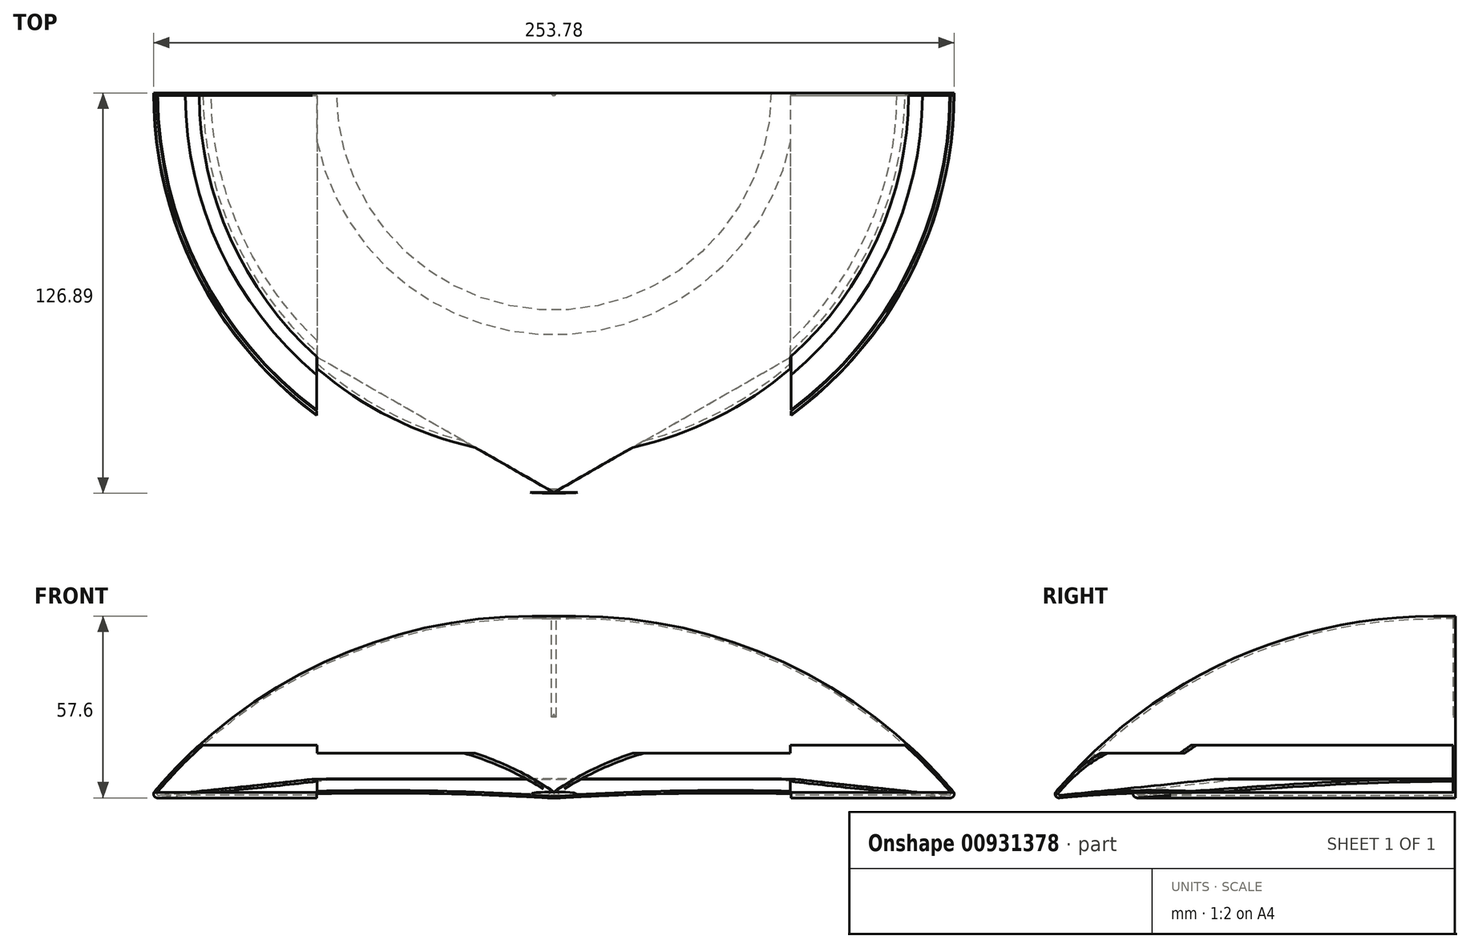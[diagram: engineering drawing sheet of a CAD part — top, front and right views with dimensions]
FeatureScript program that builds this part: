
annotation { "Feature Type Name" : "Feature", "Feature Type Description" : "" }
export const myFeature = defineFeature(function(context is Context, id is Id, definition is map)
    precondition{}
    {
        {
            var Q0;
            Q0=qCreatedBy(makeId("Right.planeOp"),FACE);
            var sketch = newSketch(context, id + "F0", { "sketchPlane" : qUnion([Q0])});
            skLineSegment(sketch, "E0", {"start": v(0, 0) * mm, "end": v(0, 55) * mm});
            skLineSegment(sketch, "E1", {"start": v(0, 0) * mm, "end": v(-107.97, 0) * mm});
            skArc(sketch, "E2", {"start": v(0, 55) * mm, "mid": v(-68.84, 41.9) * mm, "end": v(-125, 0) * mm});
            skLineSegment(sketch, "E3", {"start": v(0, 15) * mm, "end": v(0, 25) * mm});
            skLineSegment(sketch, "E4", {"start": v(-125, 0) * mm, "end": v(-75.8, 15) * mm});
            skLineSegment(sketch, "E5", {"start": v(-65.8, 25) * mm, "end": v(-75.8, 38.63) * mm});
            skLineSegment(sketch, "E6", {"start": v(0, 55) * mm, "end": v(-15, 40.73) * mm});
            skFitSpline(sketch, "E7", {"points": [v(-15, 40.73) * mm, v(-65.8, 25) * mm, v(-75.8, 15) * mm], "startDerivative": vector(-92.7, -22.01) * mm, "endDerivative": vector(-21.33, -30.33) * mm});
            skPoint(sketch, "E8.start.orphan", {"position": v(-125, 25) * mm});
            skPoint(sketch, "E9.end.orphan", {"position": v(-125, 15) * mm});
            skPoint(sketch, "E10.end.orphan", {"position": v(-15, 25) * mm});
            skArc(sketch, "E11.0", {"start": v(0.8, 55.77) * mm, "mid": v(-69, 42.71) * mm, "end": v(-125.87, 0.21) * mm});
            skLineSegment(sketch, "E11.1", {"start": v(0.8, -0.8) * mm, "end": v(0.8, 55.77) * mm});
            skLineSegment(sketch, "E11.2", {"start": v(0.8, -0.8) * mm, "end": v(-115.99, -0.8) * mm});
            skFitSpline(sketch, "E12", {"points": [v(-124.74, -0.86) * mm, v(-16.54, 15) * mm, v(0, 25) * mm], "startDerivative": vector(188.12, 18.56) * mm, "endDerivative": vector(41.4, 35.45) * mm});
            skFitSpline(sketch, "E13.0", {"points": [v(-124.66, -1.66) * mm, v(-116.82, -0.88) * mm, v(-101.14, 0.66) * mm, v(-78.43, 3.08) * mm, v(-60.86, 5.25) * mm, v(-48.01, 7.13) * mm, v(-39.09, 8.62) * mm, v(-30.97, 10.2) * mm, v(-24.96, 11.62) * mm, v(-20.65, 12.8) * mm, v(-17.68, 13.74) * mm, v(-14.99, 14.7) * mm, v(-11.76, 16.03) * mm, v(-8.33, 17.77) * mm, v(-4.95, 19.94) * mm, v(-2.08, 22.17) * mm, v(-0.34, 23.65) * mm, v(0.52, 24.4) * mm]});
            skLineSegment(sketch, "E14.trimOffspring", {"start": v(-107.97, 0) * mm, "end": v(-62.5, 0) * mm});
            skLineSegment(sketch, "E15", {"start": v(0.52, 24.4) * mm, "end": v(0.8, 25) * mm});
            skArc(sketch, "E16", {"start": v(-125, 0) * mm, "mid": v(-125.05, -0.49) * mm, "end": v(-124.74, -0.86) * mm});
            skArc(sketch, "E17", {"start": v(-125.87, 0.21) * mm, "mid": v(-125.9, -1.13) * mm, "end": v(-124.66, -1.66) * mm});
            skLineSegment(sketch, "E18", {"start": v(0.8, 55.77) * mm, "end": v(0.8, 25) * mm});
            skFitSpline(sketch, "E19", {"points": [v(-124.12, -0.8) * mm, v(-75.8, 4.25) * mm, v(0, 0) * mm, v(0.8, -0.8) * mm], "startDerivative": vector(93.54, 16.79) * mm, "endDerivative": vector(3.82, -12.52) * mm});
            skSolve(sketch);
        }
        {
            var Q0;
            Q0=makeQuery(id+"F0.imprint","IMPRINT",FACE,{"disambiguationData":[TD([[makeQuery(id+"F0.imprint","IMPRINT",EDGE,{"derivedFrom":sQuery(id+"F0.wireOp",EDGE,"E11.0")}),1.0]])]});
            var Q1;
            Q1=sQuery(id+"F0.wireOp",EDGE,"E11.1");
            revolve(context, id + "F1", {"surfaceOperationType" : NewSurfaceOperationType.NEW, "entities" : qUnion([Q0]), "axis" : qUnion([Q1]), "revolveType" : RevolveType.SYMMETRIC, "angle" : 180 * degree});
        }
        {
            var Q0;
            Q0=qCreatedBy(makeId("Front.planeOp"),FACE);
            var sketch = newSketch(context, id + "F2", { "sketchPlane" : qUnion([Q0])});
            skLineSegment(sketch, "E20", {"start": v(0, 0) * mm, "end": v(75, 0) * mm});
            skLineSegment(sketch, "E21", {"start": v(75, 0) * mm, "end": v(-75, 0) * mm});
            skLineSegment(sketch, "E22", {"start": v(-75, 0) * mm, "end": v(-75, 15) * mm});
            skLineSegment(sketch, "E23", {"start": v(-75, 15) * mm, "end": v(0, 0) * mm});
            skLineSegment(sketch, "E24", {"start": v(75, 0) * mm, "end": v(75, 15) * mm});
            skLineSegment(sketch, "E25", {"start": v(75, 15) * mm, "end": v(0, 0) * mm});
            skLineSegment(sketch, "E26", {"start": v(-75, 15) * mm, "end": v(-133.41, 15) * mm});
            skLineSegment(sketch, "E27", {"start": v(-133.41, 15) * mm, "end": v(-133.41, 0) * mm});
            skLineSegment(sketch, "E28", {"start": v(-133.41, 0) * mm, "end": v(-75, 0) * mm});
            skLineSegment(sketch, "E29", {"start": v(75, 0) * mm, "end": v(135.85, 0) * mm});
            skLineSegment(sketch, "E30", {"start": v(135.85, 0) * mm, "end": v(135.85, 15) * mm});
            skLineSegment(sketch, "E31", {"start": v(135.85, 15) * mm, "end": v(75, 15) * mm});
            skLineSegment(sketch, "E32", {"start": v(-133.41, 0) * mm, "end": v(-133.41, -1.66) * mm});
            skLineSegment(sketch, "E33", {"start": v(-133.41, -1.66) * mm, "end": v(135.85, -1.66) * mm});
            skLineSegment(sketch, "E34", {"start": v(135.85, -1.66) * mm, "end": v(135.85, 0) * mm});
            skSolve(sketch);
        }
        {
            var Q0;
            Q0=makeQuery(id+"F2.imprint","IMPRINT",FACE,{"disambiguationData":[TD([[makeQuery(id+"F2.imprint","IMPRINT",EDGE,{"derivedFrom":sQuery(id+"F2.wireOp",EDGE,"E22")}),1.0]])]});
            var Q1;
            Q1=makeQuery(id+"F2.imprint","IMPRINT",FACE,{"disambiguationData":[TD([[makeQuery(id+"F2.imprint","IMPRINT",EDGE,{"derivedFrom":sQuery(id+"F2.wireOp",EDGE,"E24")}),-1.0]])]});
            extrude(context, id + "F3", {"entities" : qUnion([Q0, Q1]), "operationType" : NewBodyOperationType.REMOVE, "endBound" : BoundingType.THROUGH_ALL, "depth" : 25 * mm, "offsetDistance" : 25 * mm});
        }
        {
            var Q0;
            Q0=qCreatedBy(makeId("Top.planeOp"),FACE);
            var sketch = newSketch(context, id + "F4", { "sketchPlane" : qUnion([Q0])});
            skLineSegment(sketch, "E35", {"start": v(0, 0) * mm, "end": v(0, -125) * mm});
            skLineSegment(sketch, "E36", {"start": v(-75.21, -101.57) * mm, "end": v(-75.21, -125) * mm});
            skLineSegment(sketch, "E37", {"start": v(-75.21, -125.87) * mm, "end": v(0, -125.87) * mm});
            skLineSegment(sketch, "E38.MirrorCS", {"start": v(75.21, -101.57) * mm, "end": v(75.21, -125) * mm});
            skLineSegment(sketch, "E39.MirrorCS", {"start": v(75.21, -125.87) * mm, "end": v(0, -125.87) * mm});
            skLineSegment(sketch, "E40", {"start": v(-75.21, -101.57) * mm, "end": v(-75.21, -82.86) * mm});
            skLineSegment(sketch, "E41", {"start": v(-75.21, -82.86) * mm, "end": v(0, -125.87) * mm});
            skLineSegment(sketch, "E42", {"start": v(75.21, -101.57) * mm, "end": v(75.21, -82.86) * mm});
            skLineSegment(sketch, "E43", {"start": v(75.21, -82.86) * mm, "end": v(0, -125.87) * mm});
            skLineSegment(sketch, "E44", {"start": v(-75.21, -125) * mm, "end": v(-75.21, -125.87) * mm});
            skLineSegment(sketch, "E45", {"start": v(75.21, -125) * mm, "end": v(75.21, -125.87) * mm});
            skSolve(sketch);
        }
        {
            var Q0;
            Q0 = qSketchRegion(id + "F4", true);
            extrude(context, id + "F5", {"entities" : qUnion([Q0]), "operationType" : NewBodyOperationType.REMOVE, "endBound" : BoundingType.SYMMETRIC, "depth" : 25 * mm, "offsetDistance" : 25 * mm});
        }
    });
